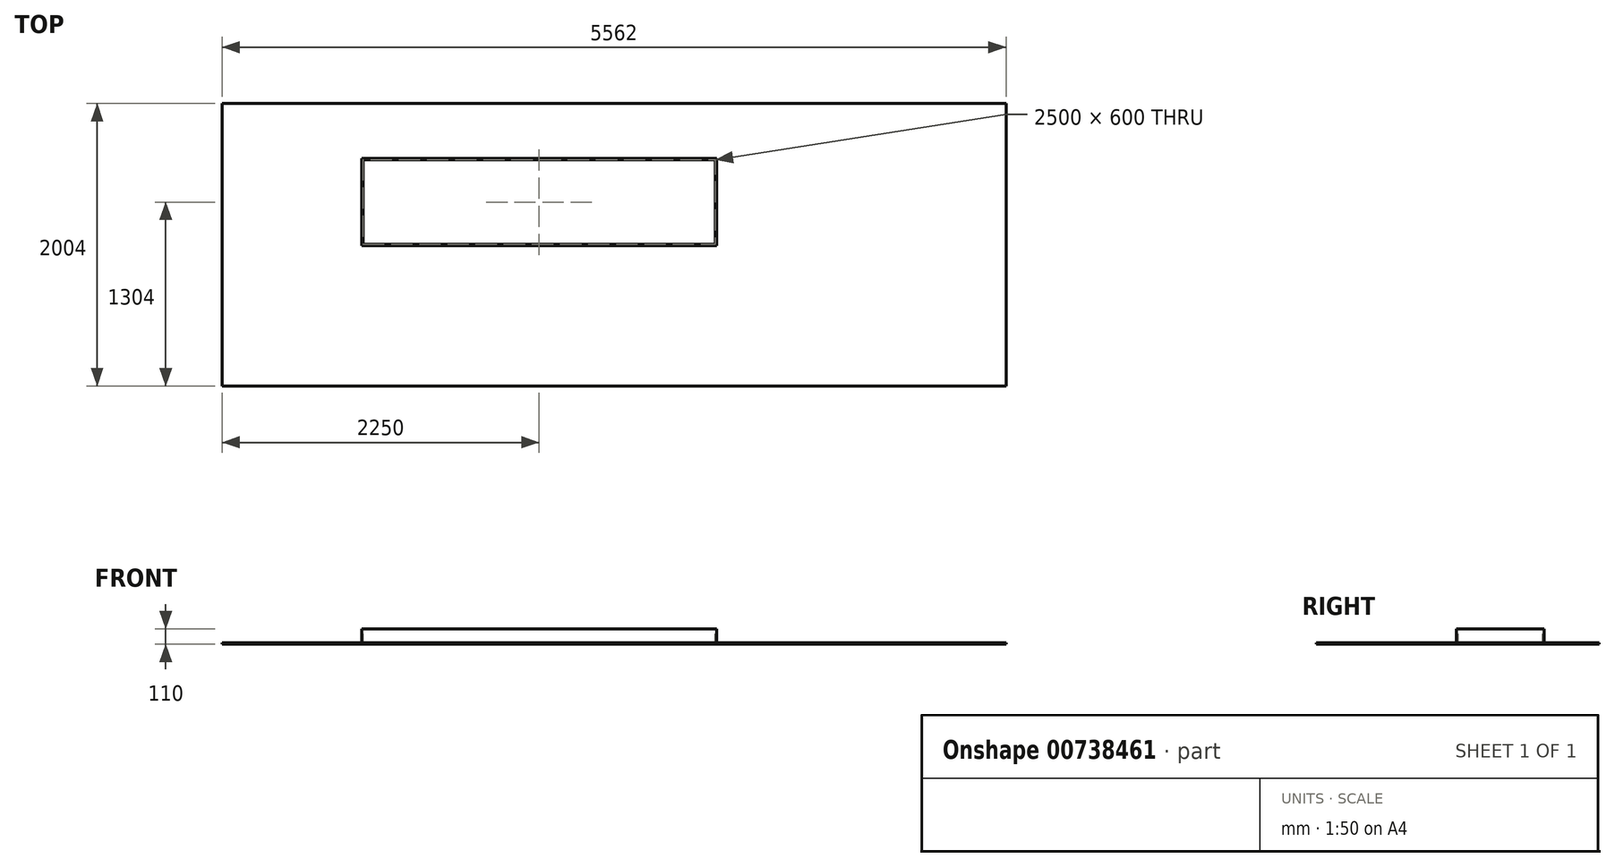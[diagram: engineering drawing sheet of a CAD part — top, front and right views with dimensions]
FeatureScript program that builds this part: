
annotation { "Feature Type Name" : "Feature", "Feature Type Description" : "" }
export const myFeature = defineFeature(function(context is Context, id is Id, definition is map)
    precondition{}
    {
        {
            var Q0;
            Q0=qCreatedBy(makeId("Top.planeOp"),FACE);
            var sketch = newSketch(context, id + "F0", { "sketchPlane" : qUnion([Q0])});
            skLineSegment(sketch, "E0.bottom", {"start": v(-5526.28, 1958.21) * mm, "end": v(35.72, 1958.21) * mm});
            skLineSegment(sketch, "E0.top", {"start": v(-5526.28, -45.79) * mm, "end": v(35.72, -45.79) * mm});
            skLineSegment(sketch, "E0.left", {"start": v(-5526.28, 1958.21) * mm, "end": v(-5526.28, -45.79) * mm});
            skLineSegment(sketch, "E0.right", {"start": v(35.72, 1958.21) * mm, "end": v(35.72, -45.79) * mm});
            skSolve(sketch);
        }
        {
            var Q0;
            Q0=makeQuery(id+"F0.imprint","IMPRINT",FACE,{"disambiguationData":[TD([[makeQuery(id+"F0.imprint","IMPRINT",EDGE,{"derivedFrom":sQuery(id+"F0.wireOp",EDGE,"E0.bottom")}),-1.0]])]});
            extrude(context, id + "F1", {"entities" : qUnion([Q0]), "depth" : 10 * mm, "offsetDistance" : 25 * mm});
        }
        {
            var Q0;
            Q0=makeQuery(id+"F1.opExtrude","CAP_FACE",FACE,{"disambiguationData":[OSD([sQuery(id+"F0.wireOp",EDGE,"E0.bottom"),sQuery(id+"F0.wireOp",EDGE,"E0.top"),sQuery(id+"F0.wireOp",EDGE,"E0.left"),sQuery(id+"F0.wireOp",EDGE,"E0.right")])],"isStart":false});
            var sketch = newSketch(context, id + "F2", { "sketchPlane" : qUnion([Q0])});
            skLineSegment(sketch, "E1.bottom", {"start": v(-4526.28, 1558.21) * mm, "end": v(-2026.28, 1558.21) * mm});
            skLineSegment(sketch, "E1.top", {"start": v(-4526.28, 958.21) * mm, "end": v(-2026.28, 958.21) * mm});
            skLineSegment(sketch, "E1.left", {"start": v(-4526.28, 1558.21) * mm, "end": v(-4526.28, 958.21) * mm});
            skLineSegment(sketch, "E1.right", {"start": v(-2026.28, 1558.21) * mm, "end": v(-2026.28, 958.21) * mm});
            skSolve(sketch);
        }
        {
            var Q0;
            Q0=makeQuery(id+"F2.imprint","IMPRINT",FACE,{"disambiguationData":[TD([[makeQuery(id+"F2.imprint","IMPRINT",EDGE,{"derivedFrom":sQuery(id+"F2.wireOp",EDGE,"E1.bottom")}),-1.0]])]});
            extrude(context, id + "F3", {"entities" : qUnion([Q0]), "operationType" : NewBodyOperationType.REMOVE, "oppositeDirection" : true, "depth" : 25 * mm, "offsetDistance" : 25 * mm});
        }
        {
            var Q0;
            Q0=makeQuery(id+"F1.opExtrude","CAP_FACE",FACE,{"disambiguationData":[OSD([sQuery(id+"F0.wireOp",EDGE,"E0.bottom"),sQuery(id+"F0.wireOp",EDGE,"E0.top"),sQuery(id+"F0.wireOp",EDGE,"E0.left"),sQuery(id+"F0.wireOp",EDGE,"E0.right")])],"isStart":false});
            var sketch = newSketch(context, id + "F4", { "sketchPlane" : qUnion([Q0])});
            skLineSegment(sketch, "E2.bottom", {"start": v(-4536.28, 1568.21) * mm, "end": v(-2016.28, 1568.21) * mm});
            skLineSegment(sketch, "E2.top", {"start": v(-4536.28, 948.21) * mm, "end": v(-2016.28, 948.21) * mm});
            skLineSegment(sketch, "E2.left", {"start": v(-4536.28, 1568.21) * mm, "end": v(-4536.28, 948.21) * mm});
            skLineSegment(sketch, "E2.right", {"start": v(-2016.28, 1568.21) * mm, "end": v(-2016.28, 948.21) * mm});
            skLineSegment(sketch, "E3.0", {"start": v(-4526.28, 1558.21) * mm, "end": v(-2026.28, 1558.21) * mm});
            skLineSegment(sketch, "E4.0", {"start": v(-4526.28, 1558.21) * mm, "end": v(-4526.28, 958.21) * mm});
            skLineSegment(sketch, "E5.0", {"start": v(-4526.28, 958.21) * mm, "end": v(-2026.28, 958.21) * mm});
            skLineSegment(sketch, "E6.0", {"start": v(-2026.28, 1558.21) * mm, "end": v(-2026.28, 958.21) * mm});
            skSolve(sketch);
        }
        {
            var Q0;
            Q0 = qSketchRegion(id + "F4", true);
            extrude(context, id + "F5", {"entities" : qUnion([Q0]), "operationType" : NewBodyOperationType.ADD, "depth" : 100 * mm, "offsetDistance" : 25 * mm});
        }
    });
